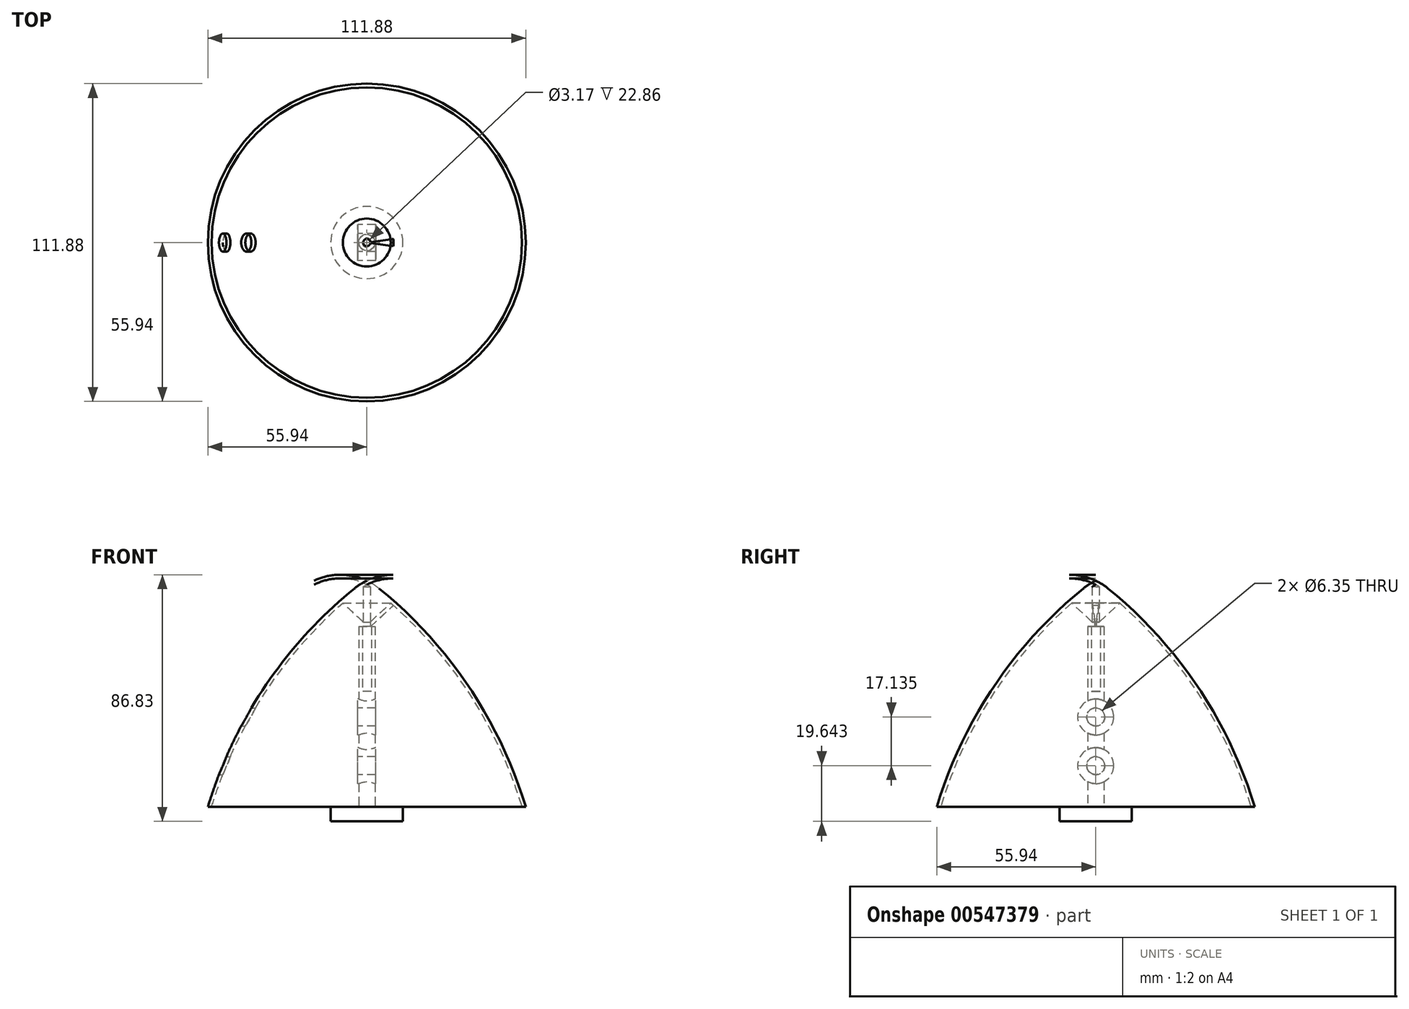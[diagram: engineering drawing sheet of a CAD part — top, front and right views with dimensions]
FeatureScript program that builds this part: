
annotation { "Feature Type Name" : "Feature", "Feature Type Description" : "" }
export const myFeature = defineFeature(function(context is Context, id is Id, definition is map)
    precondition{}
    {
        {
            var Q0;
            Q0=qCreatedBy(makeId("Front.planeOp"),FACE);
            var sketch = newSketch(context, id + "F0", { "sketchPlane" : qUnion([Q0])});
            skArc(sketch, "E0", {"start": v(55.94, 0) * mm, "mid": v(35.9, 42.35) * mm, "end": v(4.3, 76.94) * mm});
            skPoint(sketch, "E1.visualSharp", {"position": v(0.44, 79.97) * mm});
            skArc(sketch, "E1.filletArc", {"start": v(4.3, 76.94) * mm, "mid": v(2.23, 78.42) * mm, "end": v(0, 79.65) * mm});
            skArc(sketch, "E2.0", {"start": v(5.04, 74.57) * mm, "mid": v(2.66, 76.6) * mm, "end": v(0, 78.24) * mm});
            skArc(sketch, "E3.0", {"start": v(54.6, 0) * mm, "mid": v(34.75, 41.8) * mm, "end": v(3.5, 75.95) * mm});
            skLineSegment(sketch, "E4", {"start": v(1.27, 77.53) * mm, "end": v(1.27, 65.13) * mm});
            skLineSegment(sketch, "E5", {"start": v(0, 55.52) * mm, "end": v(1.27, 55.5) * mm});
            skLineSegment(sketch, "E6", {"start": v(1.27, 65.13) * mm, "end": v(8.44, 71.78) * mm});
            skLineSegment(sketch, "E7", {"start": v(1.27, 63.4) * mm, "end": v(9.4, 70.93) * mm});
            skLineSegment(sketch, "E8.trimOffspring", {"start": v(1.27, 63.4) * mm, "end": v(1.27, 55.5) * mm});
            skPoint(sketch, "E9.orphan", {"position": v(-7.79, 71.18) * mm});
            skPoint(sketch, "E10.orphan", {"position": v(-8.46, 70.06) * mm});
            skLineSegment(sketch, "E11", {"start": v(0, 0) * mm, "end": v(0, 79.65) * mm});
            skPoint(sketch, "E12.end.orphan", {"position": v(-1.27, 65.13) * mm});
            skPoint(sketch, "E13.trimOffspring.start.orphan", {"position": v(-1.27, 63.4) * mm});
            skLineSegment(sketch, "E14", {"start": v(1.27, 65.13) * mm, "end": v(1.27, 63.4) * mm});
            skLineSegment(sketch, "E15", {"start": v(54.61, 0) * mm, "end": v(55.94, 0) * mm});
            skPoint(sketch, "E16.orphan", {"position": v(43.45, 0) * mm});
            skArc(sketch, "E17.trimOffspring", {"start": v(5.04, 74.57) * mm, "mid": v(3.24, 76.16) * mm, "end": v(1.27, 77.53) * mm});
            skPoint(sketch, "E18.trimOffspring.end.orphan", {"position": v(7.79, 71.18) * mm});
            skPoint(sketch, "E18.trimOffspring.start.orphan", {"position": v(8.46, 70.06) * mm});
            skSolve(sketch);
        }
        {
            var Q0;
            Q0=makeQuery(id+"F0.imprint","IMPRINT",FACE,{"disambiguationData":[TD([[makeQuery(id+"F0.imprint","IMPRINT",EDGE,{"derivedFrom":sQuery(id+"F0.wireOp",EDGE,"E0")}),1.0]])]});
            var Q1;
            {var subQ1=sQuery(id+"F0.wireOp",EDGE,"E2.0");Q1=makeQuery(id+"F0.imprint","IMPRINT",FACE,{"disambiguationData":[TD([[makeQuery(id+"F0.imprint","IMPRINT",EDGE,{"derivedFrom":subQ1}),1.0]])]});}
            var Q2;
            Q2=sQuery(id+"F0.wireOp",EDGE,"E11");
            revolve(context, id + "F1", {"entities" : qUnion([Q0, Q1]), "axis" : qUnion([Q2]), "revolveType" : RevolveType.FULL});
        }
        {
            var Q0;
            {var subQ0=sQuery(id+"F0.wireOp",EDGE,"E6");Q0=makeQuery(id+"F0.imprint","IMPRINT",FACE,{"disambiguationData":[TD([[makeQuery(id+"F0.imprint","IMPRINT",EDGE,{"derivedFrom":subQ0}),-1.0]])]});}
            var Q1;
            Q1=sQuery(id+"F0.wireOp",EDGE,"E11");
            revolve(context, id + "F2", {"entities" : qUnion([Q0]), "axis" : qUnion([Q1]), "revolveType" : RevolveType.SYMMETRIC, "angle" : 15 * degree});
        }
        {
            var Q0;
            Q0=qCreatedBy(makeId("Top.planeOp"),FACE);
            var sketch = newSketch(context, id + "F3", { "sketchPlane" : qUnion([Q0])});
            skCircle(sketch, "E19", {"center": v(0, 0) * mm, "radius": 12.7 * mm});
            skCircle(sketch, "E20.0", {"center": v(0, 0) * mm, "radius": 1.59 * mm});
            skCircle(sketch, "E21.0", {"center": v(0, 0) * mm, "radius": 2.86 * mm});
            skSolve(sketch);
        }
        {
            var Q0;
            Q0=makeQuery(id+"F3.imprint","IMPRINT",FACE,{"disambiguationData":[TD([[makeQuery(id+"F3.imprint","IMPRINT",EDGE,{"derivedFrom":sQuery(id+"F3.wireOp",EDGE,"E19")}),1.0]])]});
            var Q1;
            Q1=makeQuery(id+"F3.imprint","IMPRINT",FACE,{"disambiguationData":[TD([[makeQuery(id+"F3.imprint","IMPRINT",EDGE,{"derivedFrom":sQuery(id+"F3.wireOp",EDGE,"E20.0")}),-1.0]])]});
            var Q2;
            Q2=makeQuery(id+"F3.imprint","IMPRINT",FACE,{"disambiguationData":[TD([[makeQuery(id+"F3.imprint","IMPRINT",EDGE,{"derivedFrom":sQuery(id+"F3.wireOp",EDGE,"E20.0")}),1.0]])]});
            extrude(context, id + "F4", {"entities" : qUnion([Q0, Q1, Q2]), "oppositeDirection" : true, "depth" : 5.08 * mm, "offsetDistance" : 25.4 * mm});
        }
        {
            var Q0;
            Q0=makeQuery(id+"F3.imprint","IMPRINT",FACE,{"disambiguationData":[TD([[makeQuery(id+"F3.imprint","IMPRINT",EDGE,{"derivedFrom":sQuery(id+"F3.wireOp",EDGE,"E20.0")}),-1.0]])]});
            extrude(context, id + "F5", {"entities" : qUnion([Q0]), "operationType" : NewBodyOperationType.ADD, "depth" : 63.5 * mm, "offsetDistance" : 25.4 * mm});
        }
        {
            var Q0;
            Q0=qCreatedBy(makeId("Right.planeOp"),FACE);
            var sketch = newSketch(context, id + "F6", { "sketchPlane" : qUnion([Q0])});
            skCircle(sketch, "E22", {"center": v(0, 31.7) * mm, "radius": 3.18 * mm});
            skCircle(sketch, "E23", {"center": v(0, 31.7) * mm, "radius": 6.35 * mm});
            skCircle(sketch, "E24", {"center": v(0, 14.56) * mm, "radius": 3.18 * mm});
            skCircle(sketch, "E25", {"center": v(0, 14.56) * mm, "radius": 6.35 * mm});
            skSolve(sketch);
        }
        {
            var Q0;
            Q0=makeQuery(id+"F3.imprint","IMPRINT",FACE,{"disambiguationData":[TD([[makeQuery(id+"F3.imprint","IMPRINT",EDGE,{"derivedFrom":sQuery(id+"F3.wireOp",EDGE,"E19")}),1.0]])]});
            var sketch = newSketch(context, id + "F7", { "sketchPlane" : qUnion([Q0])});
            skCircle(sketch, "E26", {"center": v(0, 0) * mm, "radius": 1.58 * mm});
            skSolve(sketch);
        }
        {
            var Q0;
            Q0 = qSketchRegion(id + "F7", true);
            extrude(context, id + "F8", {"entities" : qUnion([Q0]), "operationType" : NewBodyOperationType.ADD, "depth" : 40.64 * mm, "offsetDistance" : 25.4 * mm});
        }
        {
            var Q0;
            Q0=makeQuery(id+"F6.imprint","IMPRINT",FACE,{"disambiguationData":[TD([[makeQuery(id+"F6.imprint","IMPRINT",EDGE,{"derivedFrom":sQuery(id+"F6.wireOp",EDGE,"E22")}),-1.0]])]});
            var Q1;
            Q1=makeQuery(id+"F6.imprint","IMPRINT",FACE,{"disambiguationData":[TD([[makeQuery(id+"F6.imprint","IMPRINT",EDGE,{"derivedFrom":sQuery(id+"F6.wireOp",EDGE,"E24")}),-1.0]])]});
            extrude(context, id + "F9", {"entities" : qUnion([Q0, Q1]), "operationType" : NewBodyOperationType.ADD, "endBound" : BoundingType.SYMMETRIC, "depth" : 6.35 * mm, "offsetDistance" : 25.4 * mm});
        }
        {
            var Q0;
            Q0=makeQuery(id+"F9.opExtrude","CAP_FACE",FACE,{"disambiguationData":[OSD([sQuery(id+"F6.wireOp",EDGE,"E22"),sQuery(id+"F6.wireOp",EDGE,"E23")])],"isStart":false});
            var sketch = newSketch(context, id + "F10", { "sketchPlane" : qUnion([Q0])});
            skCircle(sketch, "E27", {"center": v(0, 31.7) * mm, "radius": 3.18 * mm});
            skCircle(sketch, "E28.0", {"center": v(0, 14.56) * mm, "radius": 3.18 * mm});
            skSolve(sketch);
        }
        {
            var Q0;
            Q0=makeQuery(id+"F10.imprint","IMPRINT",FACE,{"disambiguationData":[TD([[makeQuery(id+"F10.imprint","IMPRINT",EDGE,{"derivedFrom":sQuery(id+"F10.wireOp",EDGE,"E28.0")}),1.0]])]});
            var Q1;
            Q1=makeQuery(id+"F10.imprint","IMPRINT",FACE,{"disambiguationData":[TD([[makeQuery(id+"F10.imprint","IMPRINT",EDGE,{"derivedFrom":makeQuery(id+"F9.opExtrude","CAP_EDGE",EDGE,{"disambiguationData":[OSD([sQuery(id+"F6.wireOp",EDGE,"E22")])],"isStart":false})}),1.0]])]});
            extrude(context, id + "F11", {"entities" : qUnion([Q0, Q1]), "operationType" : NewBodyOperationType.REMOVE, "endBound" : BoundingType.THROUGH_ALL, "oppositeDirection" : true, "depth" : 25.4 * mm, "offsetDistance" : 25.4 * mm});
        }
    });
